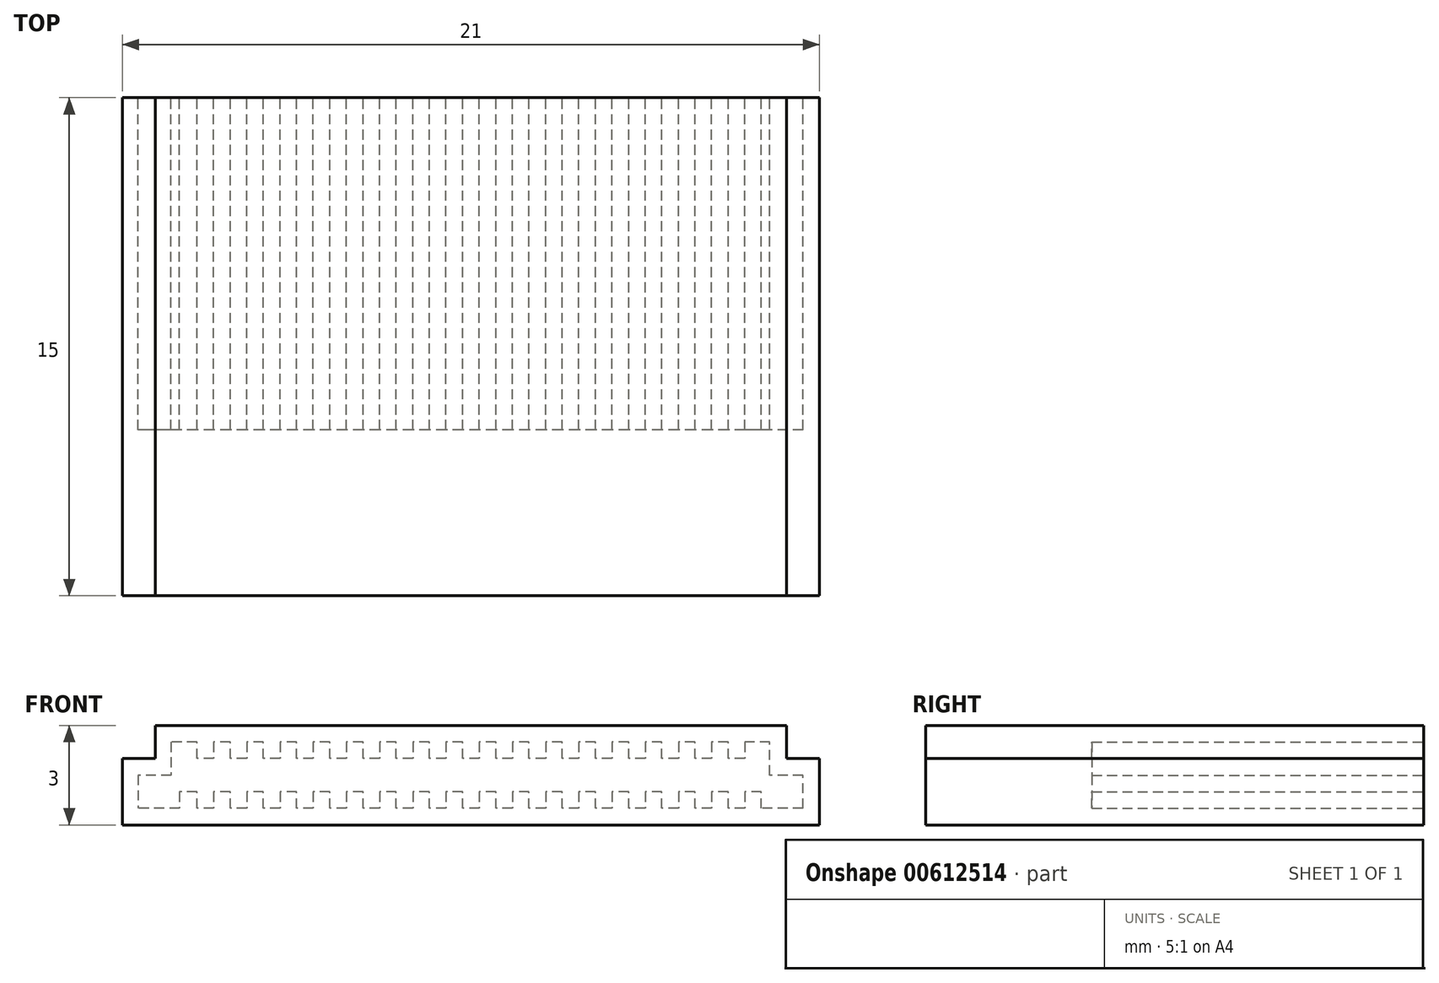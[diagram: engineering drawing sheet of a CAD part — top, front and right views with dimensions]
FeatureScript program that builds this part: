
annotation { "Feature Type Name" : "Feature", "Feature Type Description" : "" }
export const myFeature = defineFeature(function(context is Context, id is Id, definition is map)
    precondition{}
    {
        {
            var Q0;
            Q0=qCreatedBy(makeId("Front.planeOp"),FACE);
            var sketch = newSketch(context, id + "F0", { "sketchPlane" : qUnion([Q0])});
            skLineSegment(sketch, "E0", {"start": v(-7.55, 0) * mm, "end": v(-28.55, 0) * mm});
            skLineSegment(sketch, "E1", {"start": v(-7.55, 0) * mm, "end": v(-7.55, 2) * mm});
            skLineSegment(sketch, "E2", {"start": v(-7.55, 2) * mm, "end": v(-8.55, 2) * mm});
            skLineSegment(sketch, "E3", {"start": v(-8.55, 2) * mm, "end": v(-8.55, 3) * mm});
            skLineSegment(sketch, "E4", {"start": v(-8.55, 3) * mm, "end": v(-27.55, 3) * mm});
            skLineSegment(sketch, "E5", {"start": v(-27.55, 3) * mm, "end": v(-27.55, 2) * mm});
            skLineSegment(sketch, "E6", {"start": v(-27.55, 2) * mm, "end": v(-28.55, 2) * mm});
            skLineSegment(sketch, "E7", {"start": v(-28.55, 2) * mm, "end": v(-28.55, 0) * mm});
            skSolve(sketch);
        }
        {
            var Q0;
            Q0=makeQuery(id+"F0.imprint","IMPRINT",FACE,{"disambiguationData":[TD([[makeQuery(id+"F0.imprint","IMPRINT",EDGE,{"derivedFrom":sQuery(id+"F0.wireOp",EDGE,"E0")}),-1.0]])]});
            extrude(context, id + "F1", {"entities" : qUnion([Q0]), "depth" : 15 * mm, "offsetDistance" : 25 * mm});
        }
        {
            var Q0;
            Q0=makeQuery(id+"F1.opExtrude","CAP_FACE",FACE,{"disambiguationData":[OSD([sQuery(id+"F0.wireOp",EDGE,"E0"),sQuery(id+"F0.wireOp",EDGE,"E1"),sQuery(id+"F0.wireOp",EDGE,"E2"),sQuery(id+"F0.wireOp",EDGE,"E3"),sQuery(id+"F0.wireOp",EDGE,"E4"),sQuery(id+"F0.wireOp",EDGE,"E5"),sQuery(id+"F0.wireOp",EDGE,"E6"),sQuery(id+"F0.wireOp",EDGE,"E7")])],"isStart":true});
            var sketch = newSketch(context, id + "F2", { "sketchPlane" : qUnion([Q0])});
            skPoint(sketch, "E8.endSnap0", {"position": v(8.05, 2) * mm});
            skPoint(sketch, "E9.endSnap0", {"position": v(28.05, 2) * mm});
            skLineSegment(sketch, "E10", {"start": v(8.05, 0.5) * mm, "end": v(8.05, 1.5) * mm});
            skLineSegment(sketch, "E11", {"start": v(8.05, 1.5) * mm, "end": v(9.05, 1.5) * mm});
            skLineSegment(sketch, "E12", {"start": v(9.05, 1.5) * mm, "end": v(9.05, 2.5) * mm});
            skLineSegment(sketch, "E13", {"start": v(27.08, 2.5) * mm, "end": v(27.08, 1.5) * mm});
            skLineSegment(sketch, "E14", {"start": v(27.08, 1.5) * mm, "end": v(28.08, 1.5) * mm});
            skLineSegment(sketch, "E15", {"start": v(28.08, 1.5) * mm, "end": v(28.08, 0.5) * mm});
            skLineSegment(sketch, "E16", {"start": v(8.05, 0.5) * mm, "end": v(9.3, 0.5) * mm});
            skLineSegment(sketch, "E17", {"start": v(9.3, 0.5) * mm, "end": v(9.3, 1) * mm});
            skLineSegment(sketch, "E18", {"start": v(9.3, 1) * mm, "end": v(9.8, 1) * mm});
            skLineSegment(sketch, "E19", {"start": v(9.8, 1) * mm, "end": v(9.8, 0.5) * mm});
            skLineSegment(sketch, "E20", {"start": v(9.8, 0.5) * mm, "end": v(10.3, 0.5) * mm});
            skLineSegment(sketch, "E21", {"start": v(10.3, 0.5) * mm, "end": v(10.3, 1) * mm});
            skLineSegment(sketch, "E22", {"start": v(10.3, 1) * mm, "end": v(10.8, 1) * mm});
            skLineSegment(sketch, "E23", {"start": v(10.8, 1) * mm, "end": v(10.8, 0.5) * mm});
            skLineSegment(sketch, "E24", {"start": v(10.8, 0.5) * mm, "end": v(11.3, 0.5) * mm});
            skLineSegment(sketch, "E25", {"start": v(11.3, 0.5) * mm, "end": v(11.3, 1) * mm});
            skLineSegment(sketch, "E26", {"start": v(11.3, 1) * mm, "end": v(11.8, 1) * mm});
            skLineSegment(sketch, "E27", {"start": v(11.8, 1) * mm, "end": v(11.8, 0.5) * mm});
            skLineSegment(sketch, "E28", {"start": v(11.8, 0.5) * mm, "end": v(12.3, 0.5) * mm});
            skLineSegment(sketch, "E29", {"start": v(12.3, 0.5) * mm, "end": v(12.3, 1) * mm});
            skLineSegment(sketch, "E30", {"start": v(12.3, 1) * mm, "end": v(12.8, 1) * mm});
            skLineSegment(sketch, "E31", {"start": v(12.8, 1) * mm, "end": v(12.8, 0.5) * mm});
            skLineSegment(sketch, "E32", {"start": v(12.8, 0.5) * mm, "end": v(13.3, 0.5) * mm});
            skLineSegment(sketch, "E33", {"start": v(13.3, 0.5) * mm, "end": v(13.3, 1) * mm});
            skLineSegment(sketch, "E34", {"start": v(13.3, 1) * mm, "end": v(13.8, 1) * mm});
            skLineSegment(sketch, "E35", {"start": v(13.8, 1) * mm, "end": v(13.8, 0.5) * mm});
            skLineSegment(sketch, "E36", {"start": v(13.8, 0.5) * mm, "end": v(14.3, 0.5) * mm});
            skLineSegment(sketch, "E37", {"start": v(14.3, 0.5) * mm, "end": v(14.3, 1) * mm});
            skLineSegment(sketch, "E38", {"start": v(14.3, 1) * mm, "end": v(14.8, 1) * mm});
            skLineSegment(sketch, "E39", {"start": v(14.8, 1) * mm, "end": v(14.8, 0.5) * mm});
            skLineSegment(sketch, "E40", {"start": v(14.8, 0.5) * mm, "end": v(15.3, 0.5) * mm});
            skLineSegment(sketch, "E41", {"start": v(15.3, 0.5) * mm, "end": v(15.3, 1) * mm});
            skLineSegment(sketch, "E42", {"start": v(15.3, 1) * mm, "end": v(15.8, 1) * mm});
            skLineSegment(sketch, "E43", {"start": v(15.8, 1) * mm, "end": v(15.8, 0.5) * mm});
            skLineSegment(sketch, "E44", {"start": v(15.8, 0.5) * mm, "end": v(16.3, 0.5) * mm});
            skLineSegment(sketch, "E45", {"start": v(16.3, 0.5) * mm, "end": v(16.3, 1) * mm});
            skLineSegment(sketch, "E46", {"start": v(16.3, 1) * mm, "end": v(16.8, 1) * mm});
            skLineSegment(sketch, "E47", {"start": v(16.8, 1) * mm, "end": v(16.8, 0.5) * mm});
            skLineSegment(sketch, "E48", {"start": v(16.8, 0.5) * mm, "end": v(17.3, 0.5) * mm});
            skLineSegment(sketch, "E49", {"start": v(17.3, 0.5) * mm, "end": v(17.3, 1) * mm});
            skLineSegment(sketch, "E50", {"start": v(17.3, 1) * mm, "end": v(17.8, 1) * mm});
            skLineSegment(sketch, "E51", {"start": v(17.8, 1) * mm, "end": v(17.8, 0.5) * mm});
            skLineSegment(sketch, "E52", {"start": v(17.8, 0.5) * mm, "end": v(18.3, 0.5) * mm});
            skLineSegment(sketch, "E53", {"start": v(18.3, 0.5) * mm, "end": v(18.3, 1) * mm});
            skLineSegment(sketch, "E54", {"start": v(18.3, 1) * mm, "end": v(18.8, 1) * mm});
            skLineSegment(sketch, "E55", {"start": v(18.8, 1) * mm, "end": v(18.8, 0.5) * mm});
            skLineSegment(sketch, "E56", {"start": v(18.8, 0.5) * mm, "end": v(19.3, 0.5) * mm});
            skLineSegment(sketch, "E57", {"start": v(19.3, 0.5) * mm, "end": v(19.3, 1) * mm});
            skLineSegment(sketch, "E58", {"start": v(19.3, 1) * mm, "end": v(19.8, 1) * mm});
            skLineSegment(sketch, "E59", {"start": v(19.8, 1) * mm, "end": v(19.8, 0.5) * mm});
            skLineSegment(sketch, "E60", {"start": v(19.8, 0.5) * mm, "end": v(20.3, 0.5) * mm});
            skPoint(sketch, "E60.endSnap0", {"position": v(19.05, 0.5) * mm});
            skLineSegment(sketch, "E61", {"start": v(20.3, 0.5) * mm, "end": v(20.3, 1) * mm});
            skLineSegment(sketch, "E62", {"start": v(20.3, 1) * mm, "end": v(20.8, 1) * mm});
            skLineSegment(sketch, "E63", {"start": v(20.8, 1) * mm, "end": v(20.8, 0.5) * mm});
            skLineSegment(sketch, "E64", {"start": v(20.8, 0.5) * mm, "end": v(21.3, 0.5) * mm});
            skLineSegment(sketch, "E65", {"start": v(21.3, 0.5) * mm, "end": v(21.3, 1) * mm});
            skLineSegment(sketch, "E66", {"start": v(21.3, 1) * mm, "end": v(21.8, 1) * mm});
            skLineSegment(sketch, "E67", {"start": v(21.8, 1) * mm, "end": v(21.8, 0.5) * mm});
            skLineSegment(sketch, "E68", {"start": v(21.8, 0.5) * mm, "end": v(22.3, 0.5) * mm});
            skLineSegment(sketch, "E69", {"start": v(22.3, 0.5) * mm, "end": v(22.3, 1) * mm});
            skLineSegment(sketch, "E70", {"start": v(22.3, 1) * mm, "end": v(22.8, 1) * mm});
            skLineSegment(sketch, "E71", {"start": v(22.8, 1) * mm, "end": v(22.8, 0.5) * mm});
            skLineSegment(sketch, "E72", {"start": v(22.8, 0.5) * mm, "end": v(23.3, 0.5) * mm});
            skLineSegment(sketch, "E73", {"start": v(23.3, 0.5) * mm, "end": v(23.3, 1) * mm});
            skLineSegment(sketch, "E74", {"start": v(23.3, 1) * mm, "end": v(23.8, 1) * mm});
            skLineSegment(sketch, "E75", {"start": v(23.8, 1) * mm, "end": v(23.8, 0.5) * mm});
            skLineSegment(sketch, "E76", {"start": v(23.8, 0.5) * mm, "end": v(24.3, 0.5) * mm});
            skLineSegment(sketch, "E77", {"start": v(24.3, 0.5) * mm, "end": v(24.3, 1) * mm});
            skLineSegment(sketch, "E78", {"start": v(24.3, 1) * mm, "end": v(24.8, 1) * mm});
            skLineSegment(sketch, "E79", {"start": v(24.8, 1) * mm, "end": v(24.8, 0.5) * mm});
            skLineSegment(sketch, "E80", {"start": v(24.8, 0.5) * mm, "end": v(25.3, 0.5) * mm});
            skLineSegment(sketch, "E81", {"start": v(25.3, 0.5) * mm, "end": v(25.3, 1) * mm});
            skLineSegment(sketch, "E82", {"start": v(25.3, 1) * mm, "end": v(25.8, 1) * mm});
            skLineSegment(sketch, "E83", {"start": v(25.8, 1) * mm, "end": v(25.8, 0.5) * mm});
            skLineSegment(sketch, "E84", {"start": v(25.8, 0.5) * mm, "end": v(26.3, 0.5) * mm});
            skLineSegment(sketch, "E85", {"start": v(26.3, 0.5) * mm, "end": v(26.3, 1) * mm});
            skLineSegment(sketch, "E86", {"start": v(26.3, 1) * mm, "end": v(26.83, 1) * mm});
            skLineSegment(sketch, "E87", {"start": v(26.83, 1) * mm, "end": v(26.83, 0.5) * mm});
            skLineSegment(sketch, "E88", {"start": v(26.83, 0.5) * mm, "end": v(28.08, 0.5) * mm});
            skLineSegment(sketch, "E89", {"start": v(9.05, 2.5) * mm, "end": v(9.8, 2.5) * mm});
            skLineSegment(sketch, "E90", {"start": v(9.8, 2.5) * mm, "end": v(9.8, 2) * mm});
            skLineSegment(sketch, "E91", {"start": v(9.8, 2) * mm, "end": v(10.3, 2) * mm});
            skLineSegment(sketch, "E92", {"start": v(10.3, 2) * mm, "end": v(10.3, 2.5) * mm});
            skLineSegment(sketch, "E93", {"start": v(10.3, 2.5) * mm, "end": v(10.8, 2.5) * mm});
            skLineSegment(sketch, "E94", {"start": v(10.8, 2.5) * mm, "end": v(10.8, 2) * mm});
            skLineSegment(sketch, "E95", {"start": v(10.8, 2) * mm, "end": v(11.3, 2) * mm});
            skLineSegment(sketch, "E96", {"start": v(11.3, 2) * mm, "end": v(11.3, 2.5) * mm});
            skLineSegment(sketch, "E97", {"start": v(11.3, 2.5) * mm, "end": v(11.8, 2.5) * mm});
            skLineSegment(sketch, "E98", {"start": v(11.8, 2.5) * mm, "end": v(11.8, 2) * mm});
            skLineSegment(sketch, "E99", {"start": v(11.8, 2) * mm, "end": v(12.3, 2) * mm});
            skLineSegment(sketch, "E100", {"start": v(12.3, 2) * mm, "end": v(12.3, 2.5) * mm});
            skLineSegment(sketch, "E101", {"start": v(12.3, 2.5) * mm, "end": v(12.8, 2.5) * mm});
            skLineSegment(sketch, "E102", {"start": v(12.8, 2.5) * mm, "end": v(12.8, 2) * mm});
            skLineSegment(sketch, "E103", {"start": v(12.8, 2) * mm, "end": v(13.3, 2) * mm});
            skLineSegment(sketch, "E104", {"start": v(13.3, 2) * mm, "end": v(13.3, 2.5) * mm});
            skLineSegment(sketch, "E105", {"start": v(13.3, 2.5) * mm, "end": v(13.8, 2.5) * mm});
            skLineSegment(sketch, "E106", {"start": v(13.8, 2.5) * mm, "end": v(13.8, 2) * mm});
            skLineSegment(sketch, "E107", {"start": v(13.8, 2) * mm, "end": v(14.3, 2) * mm});
            skLineSegment(sketch, "E108", {"start": v(14.3, 2) * mm, "end": v(14.3, 2.5) * mm});
            skLineSegment(sketch, "E109", {"start": v(14.3, 2.5) * mm, "end": v(14.8, 2.5) * mm});
            skLineSegment(sketch, "E110", {"start": v(14.8, 2.5) * mm, "end": v(14.8, 2) * mm});
            skLineSegment(sketch, "E111", {"start": v(14.8, 2) * mm, "end": v(15.3, 2) * mm});
            skLineSegment(sketch, "E112", {"start": v(15.3, 2) * mm, "end": v(15.3, 2.5) * mm});
            skLineSegment(sketch, "E113", {"start": v(15.3, 2.5) * mm, "end": v(15.8, 2.5) * mm});
            skLineSegment(sketch, "E114", {"start": v(15.8, 2.5) * mm, "end": v(15.8, 2) * mm});
            skLineSegment(sketch, "E115", {"start": v(15.8, 2) * mm, "end": v(16.3, 2) * mm});
            skLineSegment(sketch, "E116", {"start": v(16.3, 2) * mm, "end": v(16.3, 2.5) * mm});
            skLineSegment(sketch, "E117", {"start": v(16.3, 2.5) * mm, "end": v(16.8, 2.5) * mm});
            skLineSegment(sketch, "E118", {"start": v(16.8, 2.5) * mm, "end": v(16.8, 2) * mm});
            skLineSegment(sketch, "E119", {"start": v(16.8, 2) * mm, "end": v(17.3, 2) * mm});
            skLineSegment(sketch, "E120", {"start": v(17.3, 2) * mm, "end": v(17.3, 2.5) * mm});
            skLineSegment(sketch, "E121", {"start": v(17.3, 2.5) * mm, "end": v(17.8, 2.5) * mm});
            skLineSegment(sketch, "E122", {"start": v(17.8, 2.5) * mm, "end": v(17.8, 2) * mm});
            skLineSegment(sketch, "E123", {"start": v(17.8, 2) * mm, "end": v(18.3, 2) * mm});
            skLineSegment(sketch, "E124", {"start": v(18.3, 2) * mm, "end": v(18.3, 2.5) * mm});
            skLineSegment(sketch, "E125", {"start": v(18.3, 2.5) * mm, "end": v(18.8, 2.5) * mm});
            skLineSegment(sketch, "E126", {"start": v(18.8, 2.5) * mm, "end": v(18.8, 2) * mm});
            skLineSegment(sketch, "E127", {"start": v(18.8, 2) * mm, "end": v(19.3, 2) * mm});
            skLineSegment(sketch, "E128", {"start": v(19.3, 2) * mm, "end": v(19.3, 2.5) * mm});
            skLineSegment(sketch, "E129", {"start": v(19.3, 2.5) * mm, "end": v(19.8, 2.5) * mm});
            skLineSegment(sketch, "E130", {"start": v(19.8, 2.5) * mm, "end": v(19.8, 2) * mm});
            skLineSegment(sketch, "E131", {"start": v(19.8, 2) * mm, "end": v(20.3, 2) * mm});
            skLineSegment(sketch, "E132", {"start": v(20.3, 2) * mm, "end": v(20.3, 2.5) * mm});
            skLineSegment(sketch, "E133", {"start": v(20.3, 2.5) * mm, "end": v(20.8, 2.5) * mm});
            skLineSegment(sketch, "E134", {"start": v(20.8, 2.5) * mm, "end": v(20.8, 2) * mm});
            skLineSegment(sketch, "E135", {"start": v(20.8, 2) * mm, "end": v(21.3, 2) * mm});
            skLineSegment(sketch, "E136", {"start": v(21.3, 2) * mm, "end": v(21.3, 2.5) * mm});
            skLineSegment(sketch, "E137", {"start": v(21.3, 2.5) * mm, "end": v(21.8, 2.5) * mm});
            skLineSegment(sketch, "E138", {"start": v(21.8, 2.5) * mm, "end": v(21.8, 2) * mm});
            skLineSegment(sketch, "E139", {"start": v(21.8, 2) * mm, "end": v(22.3, 2) * mm});
            skLineSegment(sketch, "E140", {"start": v(22.3, 2) * mm, "end": v(22.3, 2.5) * mm});
            skLineSegment(sketch, "E141", {"start": v(22.3, 2.5) * mm, "end": v(22.8, 2.5) * mm});
            skLineSegment(sketch, "E142", {"start": v(22.8, 2.5) * mm, "end": v(22.8, 2) * mm});
            skLineSegment(sketch, "E143", {"start": v(22.8, 2) * mm, "end": v(23.3, 2) * mm});
            skLineSegment(sketch, "E144", {"start": v(23.3, 2) * mm, "end": v(23.3, 2.5) * mm});
            skLineSegment(sketch, "E145", {"start": v(23.3, 2.5) * mm, "end": v(23.8, 2.5) * mm});
            skLineSegment(sketch, "E146", {"start": v(23.8, 2.5) * mm, "end": v(23.8, 2) * mm});
            skLineSegment(sketch, "E147", {"start": v(23.8, 2) * mm, "end": v(24.3, 2) * mm});
            skLineSegment(sketch, "E148", {"start": v(24.3, 2) * mm, "end": v(24.3, 2.5) * mm});
            skLineSegment(sketch, "E149", {"start": v(24.3, 2.5) * mm, "end": v(24.8, 2.5) * mm});
            skLineSegment(sketch, "E150", {"start": v(24.8, 2.5) * mm, "end": v(24.8, 2) * mm});
            skLineSegment(sketch, "E151", {"start": v(24.8, 2) * mm, "end": v(25.3, 2) * mm});
            skLineSegment(sketch, "E152", {"start": v(25.3, 2) * mm, "end": v(25.3, 2.5) * mm});
            skLineSegment(sketch, "E153", {"start": v(25.3, 2.5) * mm, "end": v(25.8, 2.5) * mm});
            skLineSegment(sketch, "E154", {"start": v(25.8, 2.5) * mm, "end": v(25.8, 2) * mm});
            skLineSegment(sketch, "E155", {"start": v(25.8, 2) * mm, "end": v(26.3, 2) * mm});
            skLineSegment(sketch, "E156", {"start": v(26.3, 2) * mm, "end": v(26.3, 2.5) * mm});
            skLineSegment(sketch, "E157", {"start": v(26.3, 2.5) * mm, "end": v(27.08, 2.5) * mm});
            skSolve(sketch);
        }
        {
            var Q0;
            Q0=makeQuery(id+"F2.imprint","IMPRINT",FACE,{"disambiguationData":[TD([[makeQuery(id+"F2.imprint","IMPRINT",EDGE,{"derivedFrom":sQuery(id+"F2.wireOp",EDGE,"E10")}),-1.0]])]});
            extrude(context, id + "F3", {"entities" : qUnion([Q0]), "operationType" : NewBodyOperationType.REMOVE, "oppositeDirection" : true, "depth" : 10 * mm, "offsetDistance" : 25 * mm});
        }
    });
